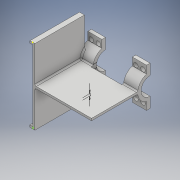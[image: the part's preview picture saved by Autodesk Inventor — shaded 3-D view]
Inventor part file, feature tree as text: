
AUTODESK INVENTOR PART (.ipt)
format: ipt  version: 2018 (Build 220112000, 112)  size: 281,600 bytes
history: native  units: mm
features: sketch x11, extrude x10, fillet x1
ambient origin geometry x8: Origin, YZ Plane, XZ Plane, XY Plane, X Axis, Y Axis, Z Axis, Center Point
bodies: Solid1 (feature_tree)
feature tree (22):
  extrude  "Extrusion1"  Depth=106.0mm
  sketch  "Sketch2"  dims[d2=80.0mm d3=3.0mm]
  sketch  "Sketch3"  dims[d4=70.0mm d5=0.0mm d6=3.0mm]
  sketch  "Sketch4"  dims[d7=3.0mm d8=3.0mm]
  extrude  "Extrusion2"  Depth=3.0mm
  extrude  "Extrusion3"  Depth=3.0mm
  extrude  "Extrusion4"  Depth=3.0mm
  extrude  "Extrusion5"  Depth=4.0mm TaperAngle=0.0deg
  extrude  "Extrusion6"  Depth=12.7mm
  extrude  "Extrusion7"  Depth=20.0mm TaperAngle=0.0deg
  fillet  "Fillet1"  Radius=20.0mm
  extrude  "Extrusion8"  Depth=15.0mm
  extrude  "Extrusion9"  Depth=15.0mm
  extrude  "Extrusion10"  Depth=5.0mm TaperAngle=0.0deg
  sketch  "Sketch1"  dims[d0=3.0mm d1=106.0mm]
  sketch  "Sketch5"  dims[d9=4.0mm d10=0.0mm d11=4.0mm d12=0.0mm]
  sketch  "Sketch6"  dims[d13=12.7mm d14=25.4mm]
  sketch  "Sketch7"  dims[d15=35.0mm d16=20.0mm d17=0.0mm d18=20.0mm d19=0.0mm]
  sketch  "Sketch8"  dims[d20=2000.0mm d21=0.0mm d22=15.0mm]
  sketch  "Sketch9"  dims[d23=15.0mm d24=15.0mm]
  sketch  "Sketch10"  dims[d25=20.0mm d26=5.0mm d27=0.0mm]
  sketch  "Sketch11"  dims[d28=2.0mm d29=7.5mm d30=0.0mm d31=6.35mm d32=6.35mm d33=6.35mm d34=6.35mm d35=7.5mm d36=0.0mm d37=6.35mm d38=6.35mm d39=6.35mm d40=6.35mm d41=7.5mm d42=0.0mm]
